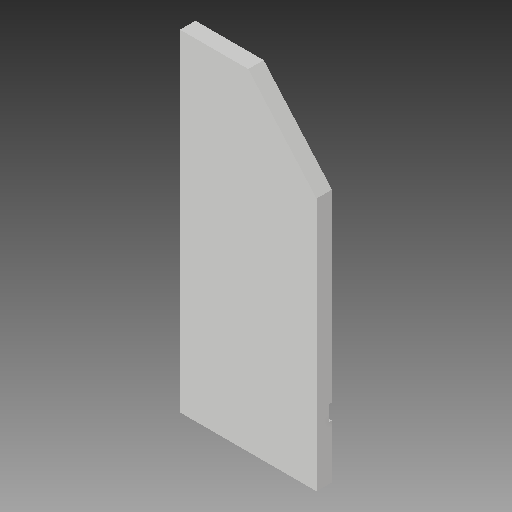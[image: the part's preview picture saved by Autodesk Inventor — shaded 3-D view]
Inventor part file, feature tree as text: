
AUTODESK INVENTOR PART (.ipt)
format: ipt  version: 2018 (Build 220112000, 112)  size: 106,496 bytes
history: native  units: mm
features: extrude x2, sketch x2, other x1
ambient origin geometry x8: Origin, YZ Plane, XZ Plane, XY Plane, X Axis, Y Axis, Z Axis, Center Point
bodies: Body1 (feature_tree)
feature tree (5):
  other  "Sólido1"
  extrude  "Extrusão1"  Depth=340.0mm
  extrude  "Extrusão3"  Depth=3.0mm
  sketch  "Esboço1"  dims[d0=140.0mm d1=340.0mm]
  sketch  "Esboço3"  dims[d2=70.0mm d3=260.0mm d4=15.88mm d5=0.0mm d11=15.98mm d12=3.0mm d13=0.0mm]
